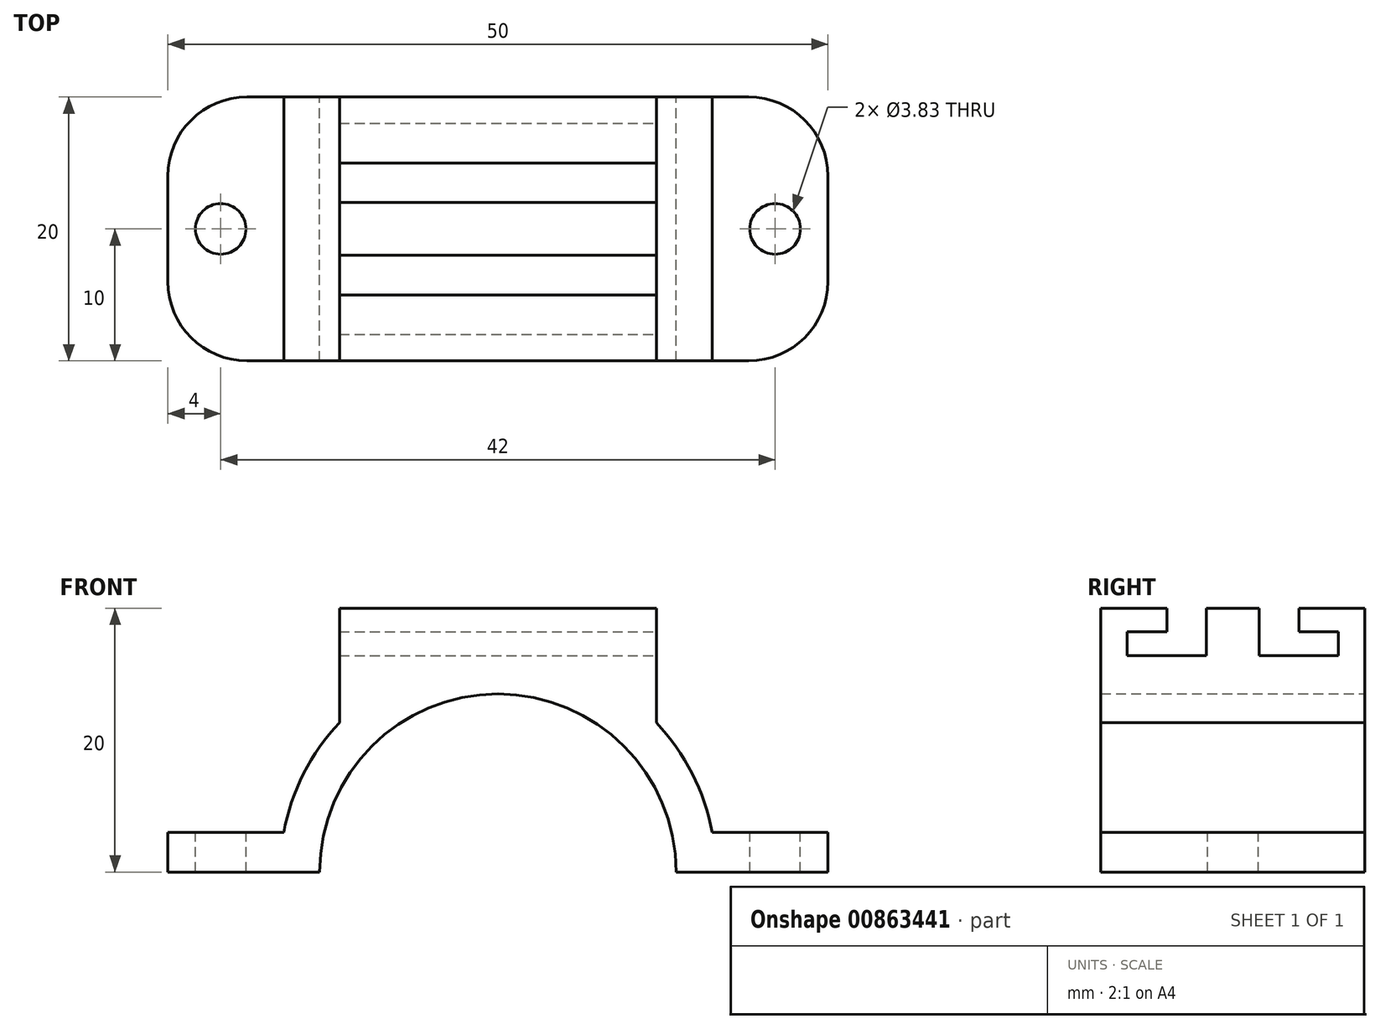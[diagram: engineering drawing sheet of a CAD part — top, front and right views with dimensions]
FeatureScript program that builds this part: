
annotation { "Feature Type Name" : "Feature", "Feature Type Description" : "" }
export const myFeature = defineFeature(function(context is Context, id is Id, definition is map)
    precondition{}
    {
        {
            var Q0;
            Q0=qCreatedBy(makeId("Front.planeOp"),FACE);
            var sketch = newSketch(context, id + "F0", { "sketchPlane" : qUnion([Q0])});
            skLineSegment(sketch, "E0.bottom", {"start": v(-25, 0) * mm, "end": v(-13.5, 0) * mm});
            skLineSegment(sketch, "E0.top", {"start": v(-25, 3) * mm, "end": v(-16.22, 3) * mm});
            skLineSegment(sketch, "E0.left", {"start": v(-25, 0) * mm, "end": v(-25, 3) * mm});
            skLineSegment(sketch, "E0.right", {"start": v(25, 0) * mm, "end": v(25, 3) * mm});
            skArc(sketch, "E1", {"start": v(16.22, 3) * mm, "mid": v(0, 16.5) * mm, "end": v(-16.22, 3) * mm});
            skArc(sketch, "E2", {"start": v(13.5, 0) * mm, "mid": v(0, 13.5) * mm, "end": v(-13.5, 0) * mm});
            skLineSegment(sketch, "E3.trimOffspring", {"start": v(16.22, 3) * mm, "end": v(25, 3) * mm});
            skLineSegment(sketch, "E4.trimOffspring", {"start": v(13.5, 0) * mm, "end": v(25, 0) * mm});
            skSolve(sketch);
        }
        {
            var Q0;
            Q0 = qSketchRegion(id + "F0", true);
            extrude(context, id + "F1", {"entities" : qUnion([Q0]), "depth" : 20 * mm, "offsetDistance" : 25 * mm});
        }
        {
            var Q0;
            Q0=makeQuery(id+"F1.opExtrude","CAP_EDGE",EDGE,{"disambiguationData":[OSD([sQuery(id+"F0.wireOp",EDGE,"E0.right")])],"isStart":false});
            var Q1;
            Q1=makeQuery(id+"F1.opExtrude","CAP_EDGE",EDGE,{"disambiguationData":[OSD([sQuery(id+"F0.wireOp",EDGE,"E0.right")])],"isStart":true});
            var Q2;
            Q2=makeQuery(id+"F1.opExtrude","CAP_EDGE",EDGE,{"disambiguationData":[OSD([sQuery(id+"F0.wireOp",EDGE,"E0.left")])],"isStart":false});
            var Q3;
            Q3=makeQuery(id+"F1.opExtrude","CAP_EDGE",EDGE,{"disambiguationData":[OSD([sQuery(id+"F0.wireOp",EDGE,"E0.left")])],"isStart":true});
            fillet(context, id + "F2", {"entities" : qUnion([Q0, Q1, Q2, Q3]), "radius" : 6 * mm, "tangentPropagation" : true, "allowEdgeOverflow" : false});
        }
        {
            var Q0;
            Q0=makeQuery(id+"F1.opExtrude","SWEPT_FACE",FACE,{"disambiguationData":[OSD([sQuery(id+"F0.wireOp",EDGE,"E0.top")])]});
            var sketch = newSketch(context, id + "F3", { "sketchPlane" : qUnion([Q0])});
            skCircle(sketch, "E5", {"center": v(-21, -10) * mm, "radius": 1.92 * mm});
            skCircle(sketch, "E6.MirrorC", {"center": v(21, -10) * mm, "radius": 1.92 * mm});
            skSolve(sketch);
        }
        {
            var Q0;
            Q0 = qSketchRegion(id + "F3", true);
            extrude(context, id + "F4", {"entities" : qUnion([Q0]), "operationType" : NewBodyOperationType.REMOVE, "oppositeDirection" : true, "depth" : 25 * mm, "offsetDistance" : 25 * mm});
        }
        {
            var Q0;
            Q0=qCreatedBy(makeId("Front.planeOp"),FACE);
            var sketch = newSketch(context, id + "F5", { "sketchPlane" : qUnion([Q0])});
            skLineSegment(sketch, "E7.top", {"start": v(-12, 20) * mm, "end": v(12, 20) * mm});
            skLineSegment(sketch, "E7.left", {"start": v(-12, 10.58) * mm, "end": v(-12, 20) * mm});
            skLineSegment(sketch, "E7.right", {"start": v(12, 10.58) * mm, "end": v(12, 20) * mm});
            skArc(sketch, "E8", {"start": v(12, 10.58) * mm, "mid": v(0, 16) * mm, "end": v(-12, 10.58) * mm});
            skSolve(sketch);
        }
        {
            var Q0;
            Q0 = qSketchRegion(id + "F5", true);
            extrude(context, id + "F6", {"entities" : qUnion([Q0]), "operationType" : NewBodyOperationType.ADD, "depth" : 20 * mm, "offsetDistance" : 25 * mm});
        }
        {
            var Q0;
            Q0=qCreatedBy(makeId("Right.planeOp"),FACE);
            var sketch = newSketch(context, id + "F7", { "sketchPlane" : qUnion([Q0])});
            skLineSegment(sketch, "E9", {"start": v(-15, 20) * mm, "end": v(-15, 18.2) * mm});
            skLineSegment(sketch, "E10", {"start": v(-15, 18.2) * mm, "end": v(-18, 18.2) * mm});
            skLineSegment(sketch, "E11", {"start": v(-18, 18.2) * mm, "end": v(-18, 16.4) * mm});
            skLineSegment(sketch, "E12", {"start": v(-18, 16.4) * mm, "end": v(-12, 16.4) * mm});
            skLineSegment(sketch, "E13", {"start": v(-12, 16.4) * mm, "end": v(-12, 20) * mm});
            skLineSegment(sketch, "E14", {"start": v(-12, 20) * mm, "end": v(-15, 20) * mm});
            skLineSegment(sketch, "E15", {"start": v(-8, 20) * mm, "end": v(-8, 16.4) * mm});
            skLineSegment(sketch, "E16", {"start": v(-8, 16.4) * mm, "end": v(-2, 16.4) * mm});
            skLineSegment(sketch, "E17", {"start": v(-2, 16.4) * mm, "end": v(-2, 18.2) * mm});
            skLineSegment(sketch, "E18", {"start": v(-2, 18.2) * mm, "end": v(-5, 18.2) * mm});
            skLineSegment(sketch, "E19", {"start": v(-5, 18.2) * mm, "end": v(-5, 20) * mm});
            skLineSegment(sketch, "E20", {"start": v(-5, 20) * mm, "end": v(-8, 20) * mm});
            skSolve(sketch);
        }
        {
            var Q0;
            Q0 = qSketchRegion(id + "F7", true);
            extrude(context, id + "F8", {"entities" : qUnion([Q0]), "operationType" : NewBodyOperationType.REMOVE, "endBound" : BoundingType.SYMMETRIC, "oppositeDirection" : true, "depth" : 25 * mm, "offsetDistance" : 25 * mm});
        }
    });
